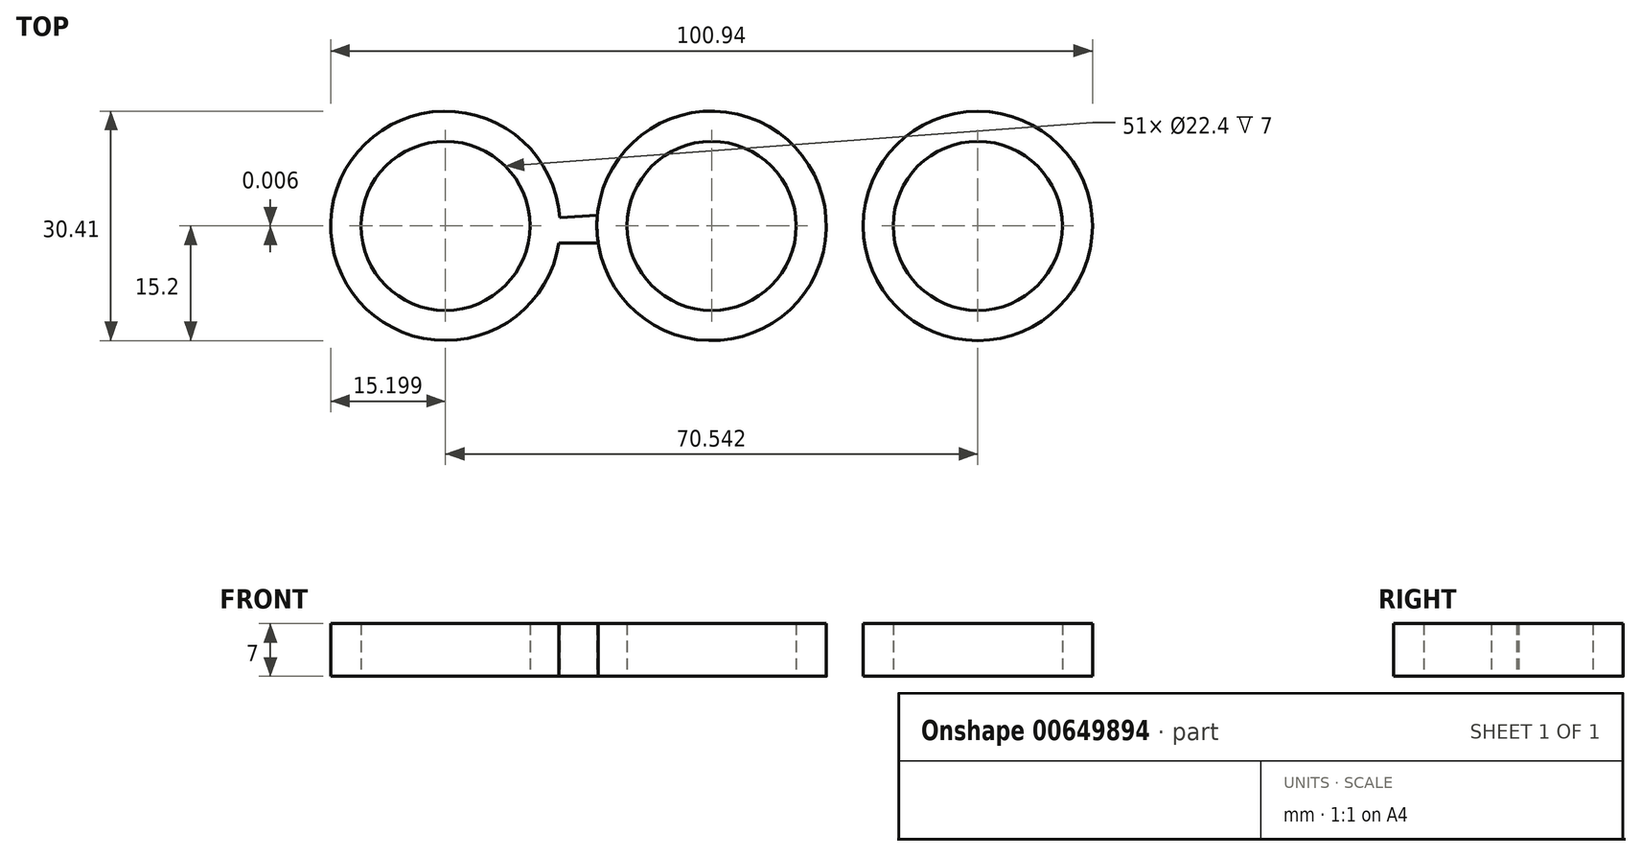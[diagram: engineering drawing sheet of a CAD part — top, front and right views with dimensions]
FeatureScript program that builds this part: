
annotation { "Feature Type Name" : "Feature", "Feature Type Description" : "" }
export const myFeature = defineFeature(function(context is Context, id is Id, definition is map)
    precondition{}
    {
        {
            var Q0;
            Q0=qCreatedBy(makeId("Top.planeOp"),FACE);
            var sketch = newSketch(context, id + "F0", { "sketchPlane" : qUnion([Q0])});
            skCircle(sketch, "E0", {"center": v(0, 0) * mm, "radius": 11.2 * mm});
            skCircle(sketch, "E1", {"center": v(0, 0) * mm, "radius": 15.2 * mm});
            skCircle(sketch, "E2", {"center": v(35.27, 0) * mm, "radius": 11.2 * mm});
            skCircle(sketch, "E3", {"center": v(35.27, 0) * mm, "radius": 15.2 * mm});
            skCircle(sketch, "E4.1.1", {"center": v(-35.27, 0) * mm, "radius": 15.2 * mm});
            skCircle(sketch, "E4.1.2", {"center": v(-35.27, 0) * mm, "radius": 11.2 * mm});
            skLineSegment(sketch, "E5", {"start": v(-20.1, 1.08) * mm, "end": v(-15.14, 1.38) * mm});
            skLineSegment(sketch, "E6", {"start": v(-20.24, -2.26) * mm, "end": v(-15.03, -2.26) * mm});
            skLineSegment(sketch, "E7.1.0", {"start": v(20.1, -1.08) * mm, "end": v(15.14, -1.38) * mm});
            skLineSegment(sketch, "E7.1.1", {"start": v(20.24, 2.26) * mm, "end": v(15.03, 2.26) * mm});
            skSolve(sketch);
        }
        {
            var Q0;
            Q0=makeQuery(id+"F0.imprint","IMPRINT",FACE,{"disambiguationData":[TD([[makeQuery(id+"F0.imprint","IMPRINT",EDGE,{"derivedFrom":sQuery(id+"F0.wireOp",EDGE,"E4.1.2")}),-1.0]])]});
            var Q1;
            Q1=makeQuery(id+"F0.imprint","IMPRINT",FACE,{"disambiguationData":[TD([[makeQuery(id+"F0.imprint","IMPRINT",EDGE,{"derivedFrom":sQuery(id+"F0.wireOp",EDGE,"E0")}),-1.0]])]});
            var Q2;
            Q2=makeQuery(id+"F0.imprint","IMPRINT",FACE,{"disambiguationData":[TD([[makeQuery(id+"F0.imprint","IMPRINT",EDGE,{"derivedFrom":sQuery(id+"F0.wireOp",EDGE,"E2")}),-1.0]])]});
            var Q3;
            {var subQ0=sQuery(id+"F0.wireOp",EDGE,"E5");var subQ1=sQuery(id+"F0.wireOp",EDGE,"E1");var subQ2=makeQuery(id+"F0.imprint","INTERSECT",VERTEX,{"derivedFrom":[subQ1,subQ0]});Q3=makeQuery(id+"F0.imprint","IMPRINT",FACE,{"disambiguationData":[TD([[makeQuery(id+"F0.imprint","IMPRINT",EDGE,{"disambiguationData":[TD([[subQ2,-1.0]])],"derivedFrom":subQ1}),-1.0]])]});}
            extrude(context, id + "F1", {"entities" : qUnion([Q0, Q1, Q2, Q3]), "depth" : 7 * mm, "offsetDistance" : 25 * mm});
        }
    });
